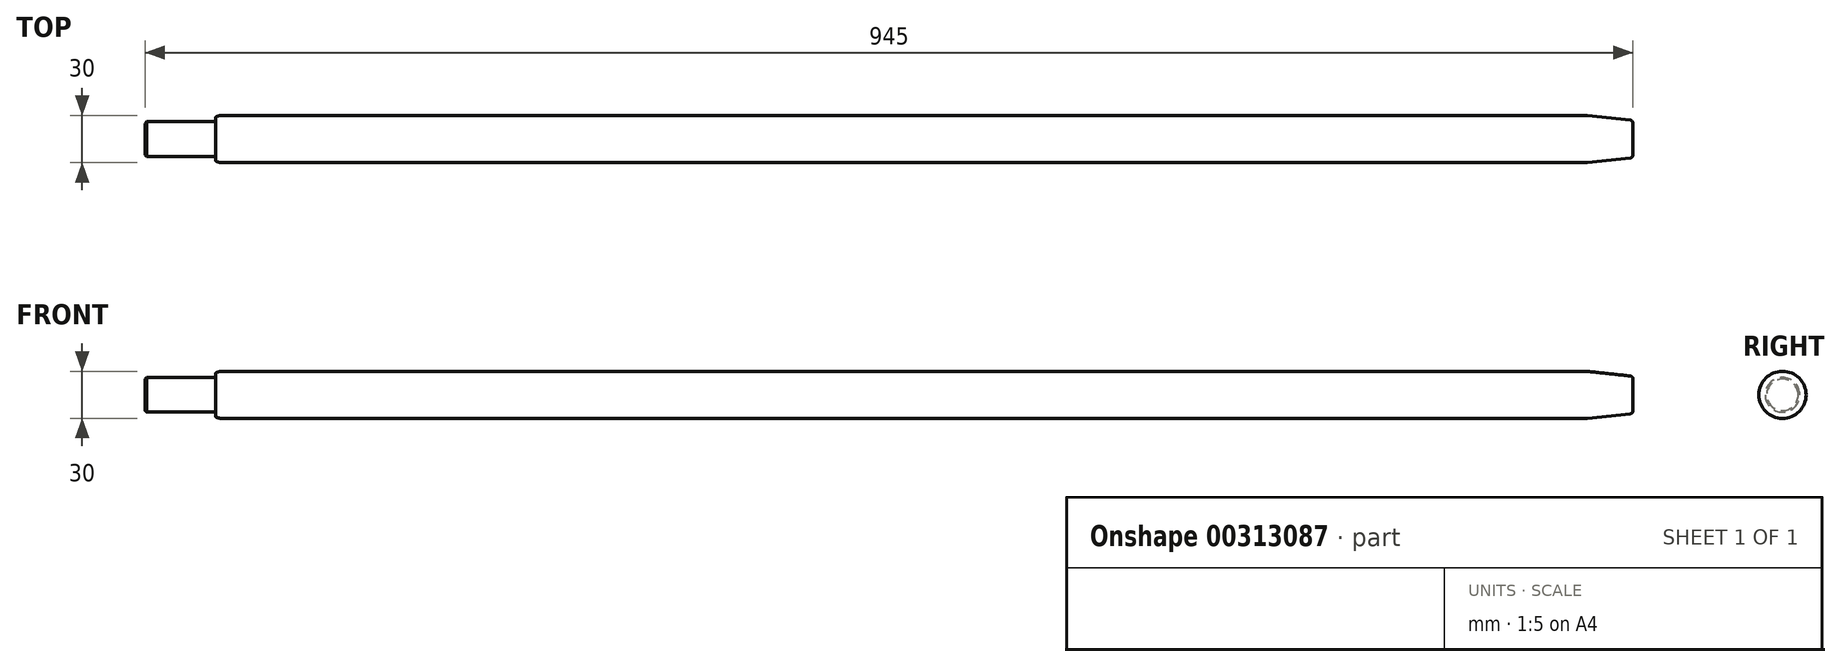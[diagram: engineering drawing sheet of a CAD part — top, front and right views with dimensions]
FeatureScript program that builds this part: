
annotation { "Feature Type Name" : "Feature", "Feature Type Description" : "" }
export const myFeature = defineFeature(function(context is Context, id is Id, definition is map)
    precondition{}
    {
        {
            var Q0;
            Q0=qCreatedBy(makeId("Right.planeOp"),FACE);
            var sketch = newSketch(context, id + "F0", { "sketchPlane" : qUnion([Q0])});
            skCircle(sketch, "E0", {"center": v(0, 0) * mm, "radius": 11 * mm});
            skSolve(sketch);
        }
        {
            var Q0;
            Q0=makeQuery(id+"F0.imprint","IMPRINT",FACE,{"disambiguationData":[TD([[makeQuery(id+"F0.imprint","IMPRINT",EDGE,{"derivedFrom":sQuery(id+"F0.wireOp",EDGE,"E0")}),1.0]])]});
            extrude(context, id + "F1", {"entities" : qUnion([Q0]), "depth" : 45 * mm});
        }
        {
            var Q0;
            Q0=makeQuery(id+"F1.opExtrude","CAP_FACE",FACE,{"disambiguationData":[OSD([sQuery(id+"F0.wireOp",EDGE,"E0")])],"isStart":false});
            var sketch = newSketch(context, id + "F2", { "sketchPlane" : qUnion([Q0])});
            skCircle(sketch, "E1", {"center": v(0, 0) * mm, "radius": 15 * mm});
            skSolve(sketch);
        }
        {
            var Q0;
            Q0=makeQuery(id+"F2.imprint","IMPRINT",FACE,{"disambiguationData":[TD([[makeQuery(id+"F2.imprint","IMPRINT",EDGE,{"derivedFrom":sQuery(id+"F2.wireOp",EDGE,"E1")}),1.0]])]});
            var Q1;
            Q1=makeQuery(id+"F2.imprint","IMPRINT",FACE,{"disambiguationData":[TD([[makeQuery(id+"F2.imprint","IMPRINT",EDGE,{"derivedFrom":makeQuery(id+"F1.opExtrude","CAP_EDGE",EDGE,{"disambiguationData":[OSD([sQuery(id+"F0.wireOp",EDGE,"E0")])],"isStart":false})}),1.0]])]});
            var Q2;
            Q2=sQuery(id+"F2.wireOp",EDGE,"E1");
            extrude(context, id + "F3", {"entities" : qUnion([Q0, Q1]), "operationType" : NewBodyOperationType.ADD, "surfaceEntities" : qUnion([Q2]), "depth" : 900 * mm});
        }
        {
            var Q0;
            Q0=makeQuery(id+"F3.opExtrude","CAP_EDGE",EDGE,{"disambiguationData":[OSD([sQuery(id+"F2.wireOp",EDGE,"E1")])],"isStart":false});
            chamfer(context, id + "F4", {"entities" : qUnion([Q0]), "chamferType" : ChamferType.OFFSET_ANGLE, "width" : 30 * mm, "oppositeDirection" : true, "angle" : 6 * degree, "tangentPropagation" : true});
        }
        {
            var Q0;
            Q0=makeQuery(id+"F1.opExtrude","CAP_EDGE",EDGE,{"disambiguationData":[OSD([sQuery(id+"F0.wireOp",EDGE,"E0")])],"isStart":true});
            chamfer(context, id + "F5", {"entities" : qUnion([Q0]), "width" : 1 * mm, "tangentPropagation" : true});
        }
        {
            var Q0;
            Q0=makeQuery(id+"F3.opExtrude","CAP_EDGE",EDGE,{"disambiguationData":[OSD([sQuery(id+"F2.wireOp",EDGE,"E1")])],"isStart":true});
            chamfer(context, id + "F6", {"entities" : qUnion([Q0]), "chamferType" : ChamferType.OFFSET_ANGLE, "width" : 3 * mm, "oppositeDirection" : false, "angle" : 15 * degree, "tangentPropagation" : true});
        }
        {
            var Q0;
            Q0=makeQuery(id+"F1.opExtrude","CAP_EDGE",EDGE,{"disambiguationData":[OSD([sQuery(id+"F0.wireOp",EDGE,"E0")])],"isStart":false});
            var Q1;
            {var subQ0=sQuery(id+"F2.wireOp",EDGE,"E1");Q1=makeQuery(id+"F6.opChamfer","BLEND_EDGE",EDGE,{"blendedFrom":[makeQuery(id+"F3.opExtrude","CAP_EDGE",EDGE,{"disambiguationData":[OSD([subQ0])],"isStart":true}),makeQuery(id+"F3.opExtrude","CAP_FACE",FACE,{"disambiguationData":[OSD([subQ0])],"isStart":true})],"blendedInto":[makeQuery(id+"F3.opExtrude","CAP_FACE",FACE,{"disambiguationData":[OSD([subQ0])],"isStart":true})]});}
            fillet(context, id + "F7", {"entities" : qUnion([Q0, Q1]), "radius" : 0.5 * mm, "tangentPropagation" : true, "allowEdgeOverflow" : false});
        }
        {
            var Q0;
            {var subQ0=sQuery(id+"F2.wireOp",EDGE,"E1");Q0=makeQuery(id+"F6.opChamfer","BLEND_EDGE",EDGE,{"blendedFrom":[makeQuery(id+"F3.opExtrude","CAP_EDGE",EDGE,{"disambiguationData":[OSD([subQ0])],"isStart":true}),makeQuery(id+"F3.opExtrude","SWEPT_FACE",FACE,{"disambiguationData":[OSD([subQ0])]})],"blendedInto":[makeQuery(id+"F3.opExtrude","SWEPT_FACE",FACE,{"disambiguationData":[OSD([subQ0])]})]});}
            fillet(context, id + "F8", {"entities" : qUnion([Q0]), "radius" : 5 * mm, "tangentPropagation" : true, "allowEdgeOverflow" : false});
        }
        {
            var Q0;
            {var subQ0=sQuery(id+"F2.wireOp",EDGE,"E1");Q0=makeQuery(id+"F4.opChamfer","BLEND_EDGE",EDGE,{"blendedFrom":[makeQuery(id+"F3.opExtrude","CAP_EDGE",EDGE,{"disambiguationData":[OSD([subQ0])],"isStart":false}),makeQuery(id+"F3.opExtrude","SWEPT_FACE",FACE,{"disambiguationData":[OSD([subQ0])]})],"blendedInto":[makeQuery(id+"F3.opExtrude","SWEPT_FACE",FACE,{"disambiguationData":[OSD([subQ0])]})]});}
            fillet(context, id + "F9", {"entities" : qUnion([Q0]), "radius" : 20 * mm, "tangentPropagation" : true, "allowEdgeOverflow" : false});
        }
        {
            var Q0;
            {var subQ0=sQuery(id+"F2.wireOp",EDGE,"E1");Q0=makeQuery(id+"F4.opChamfer","BLEND_EDGE",EDGE,{"blendedFrom":[makeQuery(id+"F3.opExtrude","CAP_EDGE",EDGE,{"disambiguationData":[OSD([subQ0])],"isStart":false}),makeQuery(id+"F3.opExtrude","CAP_FACE",FACE,{"disambiguationData":[OSD([subQ0])],"isStart":false})],"blendedInto":[makeQuery(id+"F3.opExtrude","CAP_FACE",FACE,{"disambiguationData":[OSD([subQ0])],"isStart":false})]});}
            fillet(context, id + "F10", {"entities" : qUnion([Q0]), "radius" : 2 * mm, "tangentPropagation" : true, "allowEdgeOverflow" : false});
        }
    });
